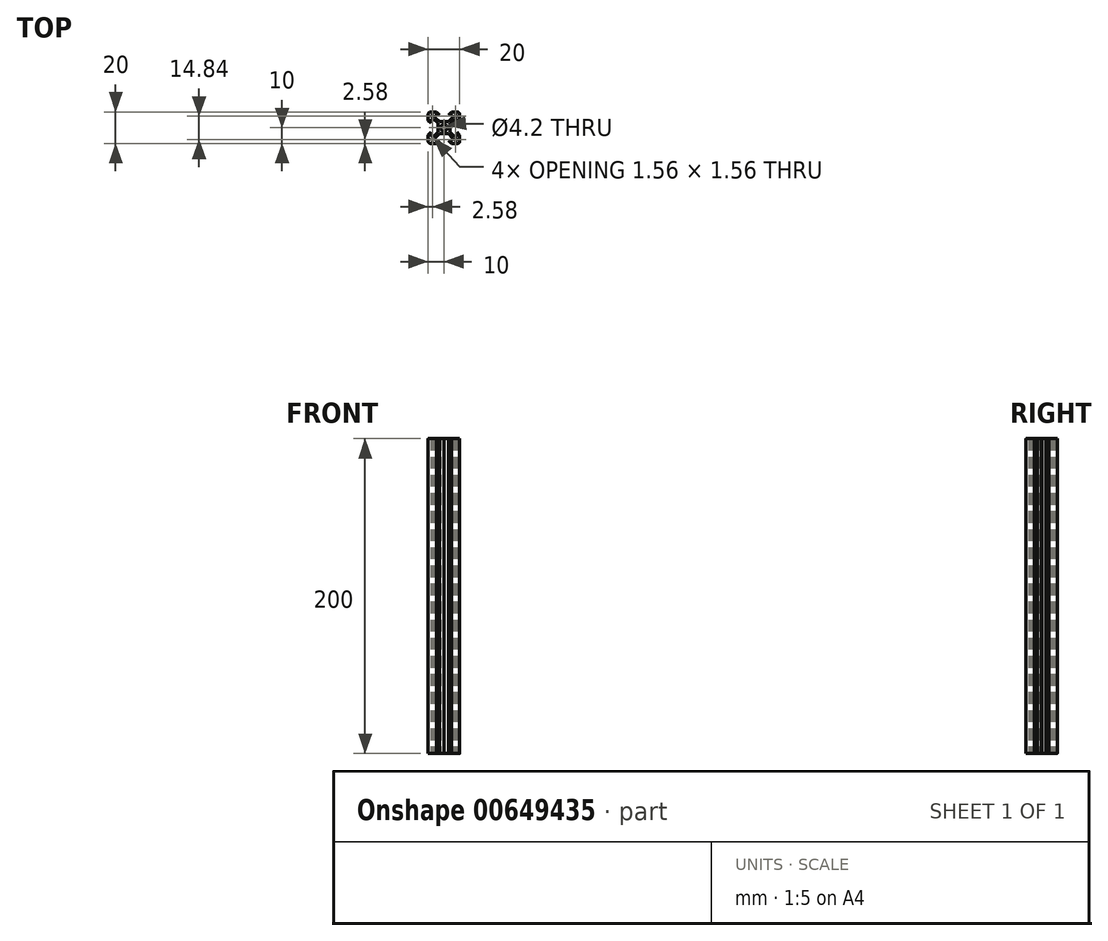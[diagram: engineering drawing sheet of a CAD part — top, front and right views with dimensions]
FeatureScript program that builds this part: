
annotation { "Feature Type Name" : "Feature", "Feature Type Description" : "" }
export const myFeature = defineFeature(function(context is Context, id is Id, definition is map)
    precondition{}
    {
        {
            var Q0;
            Q0=qCreatedBy(makeId("Top.planeOp"),FACE);
            var sketch = newSketch(context, id + "F0", { "sketchPlane" : qUnion([Q0])});
            skCircle(sketch, "E0", {"center": v(0, 0) * mm, "radius": 2.1 * mm});
            skLineSegment(sketch, "E1", {"start": v(0, 0) * mm, "end": v(0, 10) * mm, "construction": true});
            skLineSegment(sketch, "E2", {"start": v(0, 10) * mm, "end": v(8.5, 10) * mm, "construction": true});
            skLineSegment(sketch, "E3", {"start": v(10, 8.5) * mm, "end": v(10, 0) * mm, "construction": true});
            skLineSegment(sketch, "E4", {"start": v(10, 0) * mm, "end": v(0, 0) * mm, "construction": true});
            skLineSegment(sketch, "E5", {"start": v(2.84, 8.2) * mm, "end": v(4.64, 10) * mm});
            skLineSegment(sketch, "E6", {"start": v(4.64, 10) * mm, "end": v(8.5, 10) * mm});
            skLineSegment(sketch, "E7", {"start": v(10, 4.64) * mm, "end": v(8.2, 2.84) * mm});
            skLineSegment(sketch, "E8", {"start": v(8.2, 2.84) * mm, "end": v(8.2, 5.57) * mm});
            skLineSegment(sketch, "E9", {"start": v(8.2, 5.57) * mm, "end": v(6.56, 5.57) * mm});
            skLineSegment(sketch, "E10", {"start": v(6.56, 5.57) * mm, "end": v(3.83, 2.84) * mm});
            skLineSegment(sketch, "E11", {"start": v(3.83, 2.84) * mm, "end": v(3.83, 0) * mm});
            skLineSegment(sketch, "E12", {"start": v(10, 8.5) * mm, "end": v(10, 4.64) * mm});
            skLineSegment(sketch, "E13", {"start": v(2.84, 8.2) * mm, "end": v(5.57, 8.2) * mm});
            skLineSegment(sketch, "E14", {"start": v(5.57, 8.2) * mm, "end": v(5.57, 6.56) * mm});
            skLineSegment(sketch, "E15", {"start": v(5.57, 6.56) * mm, "end": v(2.84, 3.83) * mm});
            skLineSegment(sketch, "E16", {"start": v(2.84, 3.83) * mm, "end": v(0, 3.83) * mm});
            skLineSegment(sketch, "E17", {"start": v(0, 0) * mm, "end": v(10, 10) * mm, "construction": true});
            skPoint(sketch, "E18.visualSharp", {"position": v(10, 10) * mm});
            skArc(sketch, "E19.filletArc", {"start": v(10, 8.5) * mm, "mid": v(9.56, 9.56) * mm, "end": v(8.5, 10) * mm});
            skArc(sketch, "E20", {"start": v(0, 3.73) * mm, "mid": v(0.07, 3.76) * mm, "end": v(0.1, 3.83) * mm});
            skLineSegment(sketch, "E21", {"start": v(0, 3.73) * mm, "end": v(0, 2.1) * mm});
            skArc(sketch, "E22", {"start": v(3.83, 0.1) * mm, "mid": v(3.76, 0.07) * mm, "end": v(3.73, 0) * mm});
            skLineSegment(sketch, "E23", {"start": v(3.73, 0) * mm, "end": v(2.1, 0) * mm});
            skLineSegment(sketch, "E24", {"start": v(8.2, 8.2) * mm, "end": v(8.2, 6.64) * mm});
            skLineSegment(sketch, "E25", {"start": v(8.2, 6.64) * mm, "end": v(7.78, 6.64) * mm});
            skLineSegment(sketch, "E26", {"start": v(7.78, 6.64) * mm, "end": v(6.64, 7.78) * mm});
            skLineSegment(sketch, "E27", {"start": v(6.64, 7.78) * mm, "end": v(6.64, 8.2) * mm});
            skLineSegment(sketch, "E28", {"start": v(6.64, 8.2) * mm, "end": v(8.2, 8.2) * mm});
            skPoint(sketch, "E29.1.0", {"position": v(-10, 10) * mm});
            skLineSegment(sketch, "E29.1.1", {"start": v(0, 0) * mm, "end": v(-10, 10) * mm, "construction": true});
            skLineSegment(sketch, "E29.1.2", {"start": v(-5.57, 6.56) * mm, "end": v(-2.84, 3.83) * mm});
            skLineSegment(sketch, "E29.1.3", {"start": v(-6.56, 5.57) * mm, "end": v(-3.83, 2.84) * mm});
            skLineSegment(sketch, "E29.1.5", {"start": v(0, 0) * mm, "end": v(-10, 0) * mm, "construction": true});
            skLineSegment(sketch, "E29.1.6", {"start": v(-10, 0) * mm, "end": v(-10, 8.5) * mm, "construction": true});
            skLineSegment(sketch, "E29.1.7", {"start": v(-8.5, 10) * mm, "end": v(0, 10) * mm, "construction": true});
            skLineSegment(sketch, "E29.1.8", {"start": v(0, 10) * mm, "end": v(0, 0) * mm, "construction": true});
            skLineSegment(sketch, "E29.1.9", {"start": v(-8.5, 10) * mm, "end": v(-4.64, 10) * mm});
            skLineSegment(sketch, "E29.1.10", {"start": v(-10, 4.64) * mm, "end": v(-10, 8.5) * mm});
            skPoint(sketch, "E29.1.11", {"position": v(-10, 10) * mm});
            skLineSegment(sketch, "E29.1.12", {"start": v(-2.84, 3.83) * mm, "end": v(0, 3.83) * mm});
            skLineSegment(sketch, "E29.1.13", {"start": v(-4.64, 10) * mm, "end": v(-2.84, 8.2) * mm});
            skLineSegment(sketch, "E29.1.14", {"start": v(-3.83, 2.84) * mm, "end": v(-3.83, 0) * mm});
            skLineSegment(sketch, "E29.1.15", {"start": v(-2.84, 8.2) * mm, "end": v(-5.57, 8.2) * mm});
            skLineSegment(sketch, "E29.1.16", {"start": v(-3.73, 0) * mm, "end": v(-2.1, 0) * mm});
            skLineSegment(sketch, "E29.1.18", {"start": v(-8.2, 2.84) * mm, "end": v(-8.2, 5.57) * mm});
            skLineSegment(sketch, "E29.1.19", {"start": v(-8.2, 2.84) * mm, "end": v(-10, 4.64) * mm});
            skLineSegment(sketch, "E29.1.20", {"start": v(-5.57, 8.2) * mm, "end": v(-5.57, 6.56) * mm});
            skLineSegment(sketch, "E29.1.21", {"start": v(-8.2, 5.57) * mm, "end": v(-6.56, 5.57) * mm});
            skLineSegment(sketch, "E29.1.22", {"start": v(-7.78, 6.64) * mm, "end": v(-8.2, 6.64) * mm});
            skLineSegment(sketch, "E29.1.23", {"start": v(-8.2, 8.2) * mm, "end": v(-6.64, 8.2) * mm});
            skLineSegment(sketch, "E29.1.24", {"start": v(-8.2, 6.64) * mm, "end": v(-8.2, 8.2) * mm});
            skLineSegment(sketch, "E29.1.25", {"start": v(-6.64, 7.78) * mm, "end": v(-7.78, 6.64) * mm});
            skArc(sketch, "E29.1.26", {"start": v(-8.5, 10) * mm, "mid": v(-9.56, 9.56) * mm, "end": v(-10, 8.5) * mm});
            skLineSegment(sketch, "E29.1.27", {"start": v(-6.64, 8.2) * mm, "end": v(-6.64, 7.78) * mm});
            skArc(sketch, "E29.1.28", {"start": v(-3.73, 0) * mm, "mid": v(-3.76, 0.07) * mm, "end": v(-3.83, 0.1) * mm});
            skArc(sketch, "E29.1.29", {"start": v(-0.1, 3.83) * mm, "mid": v(-0.07, 3.76) * mm, "end": v(0, 3.73) * mm});
            skPoint(sketch, "E29.2.0", {"position": v(-10, -10) * mm});
            skLineSegment(sketch, "E29.2.1", {"start": v(0, 0) * mm, "end": v(-10, -10) * mm, "construction": true});
            skLineSegment(sketch, "E29.2.2", {"start": v(-6.56, -5.57) * mm, "end": v(-3.83, -2.84) * mm});
            skLineSegment(sketch, "E29.2.3", {"start": v(-5.57, -6.56) * mm, "end": v(-2.84, -3.83) * mm});
            skLineSegment(sketch, "E29.2.5", {"start": v(0, 0) * mm, "end": v(0, -10) * mm, "construction": true});
            skLineSegment(sketch, "E29.2.6", {"start": v(0, -10) * mm, "end": v(-8.5, -10) * mm, "construction": true});
            skLineSegment(sketch, "E29.2.7", {"start": v(-10, -8.5) * mm, "end": v(-10, 0) * mm, "construction": true});
            skLineSegment(sketch, "E29.2.8", {"start": v(-10, 0) * mm, "end": v(0, 0) * mm, "construction": true});
            skLineSegment(sketch, "E29.2.9", {"start": v(-10, -8.5) * mm, "end": v(-10, -4.64) * mm});
            skLineSegment(sketch, "E29.2.10", {"start": v(-4.64, -10) * mm, "end": v(-8.5, -10) * mm});
            skPoint(sketch, "E29.2.11", {"position": v(-10, -10) * mm});
            skLineSegment(sketch, "E29.2.12", {"start": v(-3.83, -2.84) * mm, "end": v(-3.83, 0) * mm});
            skLineSegment(sketch, "E29.2.13", {"start": v(-10, -4.64) * mm, "end": v(-8.2, -2.84) * mm});
            skLineSegment(sketch, "E29.2.14", {"start": v(-2.84, -3.83) * mm, "end": v(0, -3.83) * mm});
            skLineSegment(sketch, "E29.2.15", {"start": v(-8.2, -2.84) * mm, "end": v(-8.2, -5.57) * mm});
            skLineSegment(sketch, "E29.2.16", {"start": v(0, -3.73) * mm, "end": v(0, -2.1) * mm});
            skLineSegment(sketch, "E29.2.17", {"start": v(-3.73, 0) * mm, "end": v(-2.1, 0) * mm});
            skLineSegment(sketch, "E29.2.18", {"start": v(-2.84, -8.2) * mm, "end": v(-5.57, -8.2) * mm});
            skLineSegment(sketch, "E29.2.19", {"start": v(-2.84, -8.2) * mm, "end": v(-4.64, -10) * mm});
            skLineSegment(sketch, "E29.2.20", {"start": v(-8.2, -5.57) * mm, "end": v(-6.56, -5.57) * mm});
            skLineSegment(sketch, "E29.2.21", {"start": v(-5.57, -8.2) * mm, "end": v(-5.57, -6.56) * mm});
            skLineSegment(sketch, "E29.2.22", {"start": v(-6.64, -7.78) * mm, "end": v(-6.64, -8.2) * mm});
            skLineSegment(sketch, "E29.2.23", {"start": v(-8.2, -8.2) * mm, "end": v(-8.2, -6.64) * mm});
            skLineSegment(sketch, "E29.2.24", {"start": v(-6.64, -8.2) * mm, "end": v(-8.2, -8.2) * mm});
            skLineSegment(sketch, "E29.2.25", {"start": v(-7.78, -6.64) * mm, "end": v(-6.64, -7.78) * mm});
            skArc(sketch, "E29.2.26", {"start": v(-10, -8.5) * mm, "mid": v(-9.56, -9.56) * mm, "end": v(-8.5, -10) * mm});
            skLineSegment(sketch, "E29.2.27", {"start": v(-8.2, -6.64) * mm, "end": v(-7.78, -6.64) * mm});
            skArc(sketch, "E29.2.28", {"start": v(0, -3.73) * mm, "mid": v(-0.07, -3.76) * mm, "end": v(-0.1, -3.83) * mm});
            skArc(sketch, "E29.2.29", {"start": v(-3.83, -0.1) * mm, "mid": v(-3.76, -0.07) * mm, "end": v(-3.73, 0) * mm});
            skPoint(sketch, "E29.3.0", {"position": v(10, -10) * mm});
            skLineSegment(sketch, "E29.3.1", {"start": v(0, 0) * mm, "end": v(10, -10) * mm, "construction": true});
            skLineSegment(sketch, "E29.3.2", {"start": v(5.57, -6.56) * mm, "end": v(2.84, -3.83) * mm});
            skLineSegment(sketch, "E29.3.3", {"start": v(6.56, -5.57) * mm, "end": v(3.83, -2.84) * mm});
            skLineSegment(sketch, "E29.3.5", {"start": v(0, 0) * mm, "end": v(10, 0) * mm, "construction": true});
            skLineSegment(sketch, "E29.3.6", {"start": v(10, 0) * mm, "end": v(10, -8.5) * mm, "construction": true});
            skLineSegment(sketch, "E29.3.7", {"start": v(8.5, -10) * mm, "end": v(0, -10) * mm, "construction": true});
            skLineSegment(sketch, "E29.3.8", {"start": v(0, -10) * mm, "end": v(0, 0) * mm, "construction": true});
            skLineSegment(sketch, "E29.3.9", {"start": v(8.5, -10) * mm, "end": v(4.64, -10) * mm});
            skLineSegment(sketch, "E29.3.10", {"start": v(10, -4.64) * mm, "end": v(10, -8.5) * mm});
            skPoint(sketch, "E29.3.11", {"position": v(10, -10) * mm});
            skLineSegment(sketch, "E29.3.12", {"start": v(2.84, -3.83) * mm, "end": v(0, -3.83) * mm});
            skLineSegment(sketch, "E29.3.13", {"start": v(4.64, -10) * mm, "end": v(2.84, -8.2) * mm});
            skLineSegment(sketch, "E29.3.14", {"start": v(3.83, -2.84) * mm, "end": v(3.83, 0) * mm});
            skLineSegment(sketch, "E29.3.15", {"start": v(2.84, -8.2) * mm, "end": v(5.57, -8.2) * mm});
            skLineSegment(sketch, "E29.3.17", {"start": v(0, -3.73) * mm, "end": v(0, -2.1) * mm});
            skLineSegment(sketch, "E29.3.18", {"start": v(8.2, -2.84) * mm, "end": v(8.2, -5.57) * mm});
            skLineSegment(sketch, "E29.3.19", {"start": v(8.2, -2.84) * mm, "end": v(10, -4.64) * mm});
            skLineSegment(sketch, "E29.3.20", {"start": v(5.57, -8.2) * mm, "end": v(5.57, -6.56) * mm});
            skLineSegment(sketch, "E29.3.21", {"start": v(8.2, -5.57) * mm, "end": v(6.56, -5.57) * mm});
            skLineSegment(sketch, "E29.3.22", {"start": v(7.78, -6.64) * mm, "end": v(8.2, -6.64) * mm});
            skLineSegment(sketch, "E29.3.23", {"start": v(8.2, -8.2) * mm, "end": v(6.64, -8.2) * mm});
            skLineSegment(sketch, "E29.3.24", {"start": v(8.2, -6.64) * mm, "end": v(8.2, -8.2) * mm});
            skLineSegment(sketch, "E29.3.25", {"start": v(6.64, -7.78) * mm, "end": v(7.78, -6.64) * mm});
            skArc(sketch, "E29.3.26", {"start": v(8.5, -10) * mm, "mid": v(9.56, -9.56) * mm, "end": v(10, -8.5) * mm});
            skLineSegment(sketch, "E29.3.27", {"start": v(6.64, -8.2) * mm, "end": v(6.64, -7.78) * mm});
            skArc(sketch, "E29.3.28", {"start": v(3.73, 0) * mm, "mid": v(3.76, -0.07) * mm, "end": v(3.83, -0.1) * mm});
            skArc(sketch, "E29.3.29", {"start": v(0.1, -3.83) * mm, "mid": v(0.07, -3.76) * mm, "end": v(0, -3.73) * mm});
            skSolve(sketch);
        }
        {
            var Q0;
            {var subQ6=sQuery(id+"F0.wireOp",EDGE,"E29.2.2");Q0=makeQuery(id+"F0.imprint","IMPRINT",FACE,{"disambiguationData":[TD([[makeQuery(id+"F0.imprint","IMPRINT",EDGE,{"derivedFrom":subQ6}),-1.0]])]});}
            var Q1;
            {var subQ6=sQuery(id+"F0.wireOp",EDGE,"E29.1.2");Q1=makeQuery(id+"F0.imprint","IMPRINT",FACE,{"disambiguationData":[TD([[makeQuery(id+"F0.imprint","IMPRINT",EDGE,{"derivedFrom":subQ6}),-1.0]])]});}
            var Q2;
            {var subQ5=sQuery(id+"F0.wireOp",EDGE,"E29.3.2");Q2=makeQuery(id+"F0.imprint","IMPRINT",FACE,{"disambiguationData":[TD([[makeQuery(id+"F0.imprint","IMPRINT",EDGE,{"derivedFrom":subQ5}),-1.0]])]});}
            var Q3;
            Q3=makeQuery(id+"F0.imprint","IMPRINT",FACE,{"disambiguationData":[TD([[makeQuery(id+"F0.imprint","IMPRINT",EDGE,{"derivedFrom":sQuery(id+"F0.wireOp",EDGE,"E5")}),-1.0]])]});
            extrude(context, id + "F1", {"entities" : qUnion([Q0, Q1, Q2, Q3]), "depth" : 200 * mm, "offsetDistance" : 25 * mm});
        }
    });
